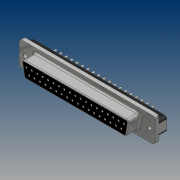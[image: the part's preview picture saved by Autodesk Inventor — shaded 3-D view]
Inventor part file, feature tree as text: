
AUTODESK INVENTOR PART (.ipt)
format: ipt  version: unknown  size: 333,824 bytes
history: native  units: mm (DEFAULTED — no unit token found)
features: sketch x6, extrude x5, projected_geometry x3, hole x1, pattern_linear x1, fillet x1
ambient origin geometry x8: Origin, YZ Plane, XZ Plane, XY Plane, X Axis, Y Axis, Z Axis, Center Point
feature tree (17):
  extrude  "Base Flange"  Depth=12.55mm
  extrude  "Socket Side Boss Housing"  Depth=1.27mm
  extrude  "Board Side Plastic Boss"  Depth=54.84mm
  hole  "Hole1"  [1 undecoded]
  extrude  "Pin Extrusion"  Depth=7.1mm
  extrude  "Socket Cut"  Depth=4.08mm TaperAngle=0.0deg
  pattern_linear  "Pin and Hole Pattern"  Spacing1=2.84mm  [1 undecoded]
  fillet  "Fillets"  Radius=0.889mm
  sketch  "Sketch1"  dims[d0=69.39mm d1=12.55mm]
  sketch  "Sketch2"  dims[d4=1.91mm d5=0.0mm d6=1.27mm]
  sketch  "Sketch3"  dims[d7=7.9mm d8=54.84mm]
  sketch  "Sketch5"  dims[d9=1.745329mm d10=1.27mm]
  sketch  "Sketch6"  dims[d11=6.17mm d12=0.0mm d13=7.1mm]
  projected_geometry  "Projected Loop1"
  projected_geometry  "Projected Loop2"
  projected_geometry  "Projected Loop3"
  sketch  "Sketch7"  dims[d15=1.27mm d16=4.08mm d17=0.0mm d23=2.84mm d25=0.889mm d26=2.77mm d27=1.385mm d28=1.42mm d29=24.93mm d30=3.18mm d31=0.0mm d32=6.1mm d33=0.0mm d34=180.0mm d36=2.77mm d37=1.0mm d38=0.5mm d39=63.5mm d40=2.156mm d41=6.0mm d42=4.0mm d43=2.0mm d44=90.0deg d45=8.0mm d46=20.594885mm]
note: 2 required parameter values undecoded (feature->parameter linkage not recoverable at this tier; creation-order binding heuristic only, values carry confidence <= 0.55)
